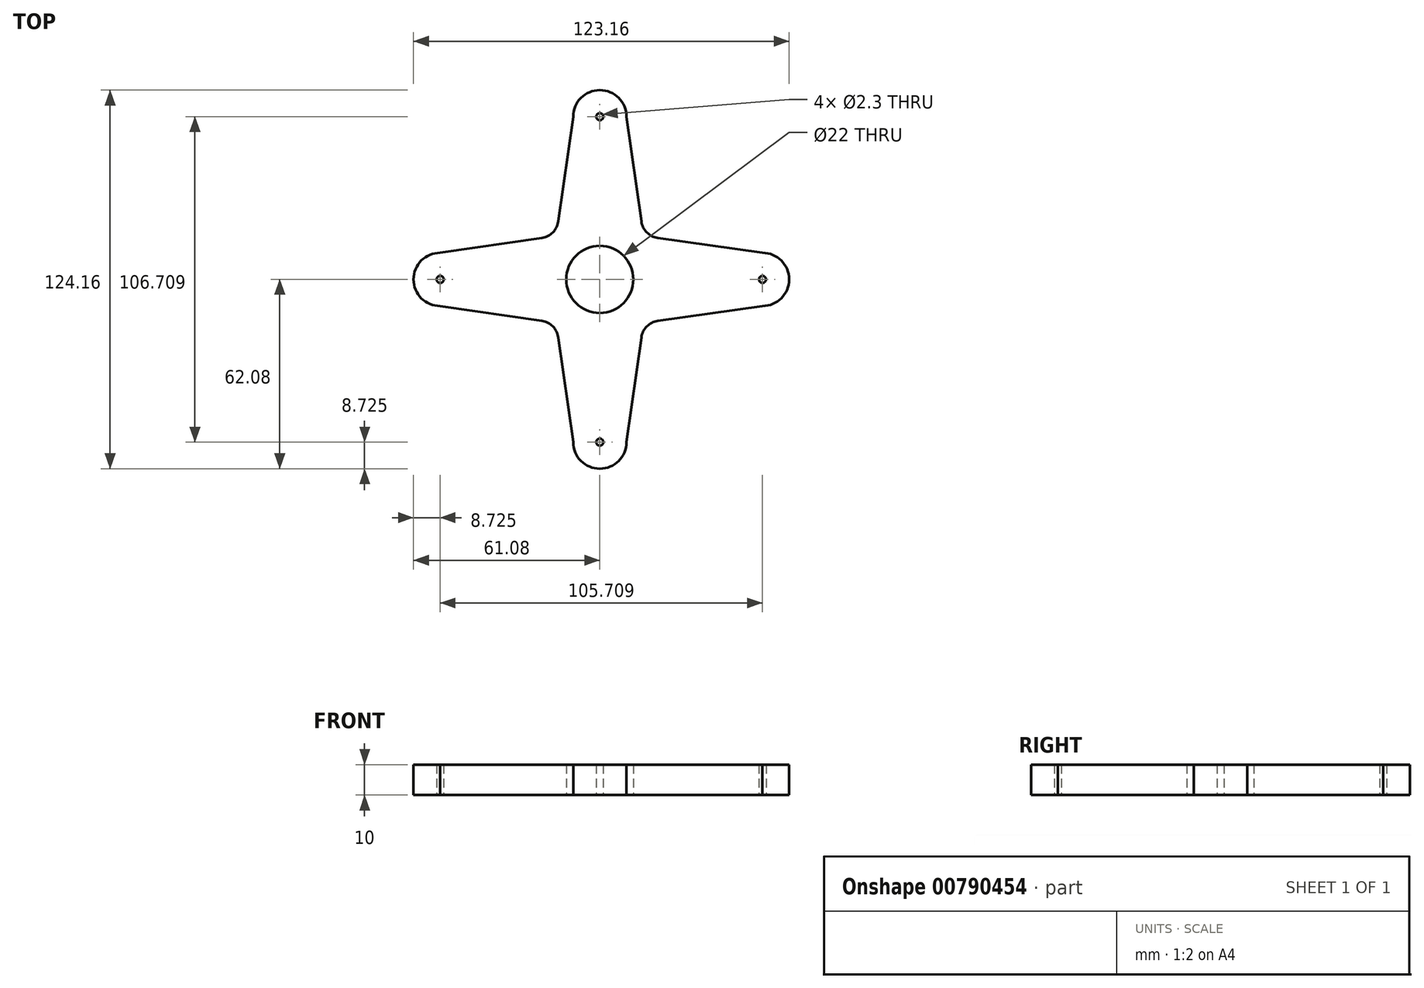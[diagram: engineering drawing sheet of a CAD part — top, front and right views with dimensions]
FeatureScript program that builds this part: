
annotation { "Feature Type Name" : "Feature", "Feature Type Description" : "" }
export const myFeature = defineFeature(function(context is Context, id is Id, definition is map)
    precondition{}
    {
        {
            var Q0;
            Q0=qCreatedBy(makeId("Top.planeOp"),FACE);
            var sketch = newSketch(context, id + "F0", { "sketchPlane" : qUnion([Q0])});
            skCircle(sketch, "E0", {"center": v(0, 0) * mm, "radius": 11 * mm});
            skCircle(sketch, "E1", {"center": v(0, 53.35) * mm, "radius": 8.73 * mm});
            skCircle(sketch, "E2.1.1", {"center": v(-52.35, 0) * mm, "radius": 8.73 * mm});
            skCircle(sketch, "E2.2.1", {"center": v(0, -53.35) * mm, "radius": 8.73 * mm});
            skCircle(sketch, "E2.3.1", {"center": v(53.35, 0) * mm, "radius": 8.73 * mm});
            skCircle(sketch, "E3", {"center": v(0, 53.35) * mm, "radius": 1.15 * mm});
            skCircle(sketch, "E4.2.0", {"center": v(0, -53.35) * mm, "radius": 1.15 * mm});
            skCircle(sketch, "E4.3.0", {"center": v(53.35, 0) * mm, "radius": 1.15 * mm});
            skLineSegment(sketch, "E5", {"start": v(8.73, 53.35) * mm, "end": v(13.62, 19) * mm});
            skLineSegment(sketch, "E6", {"start": v(-8.73, 53.35) * mm, "end": v(-13.62, 19) * mm});
            skLineSegment(sketch, "E7", {"start": v(-13.62, -19) * mm, "end": v(-8.73, -53.35) * mm});
            skLineSegment(sketch, "E8", {"start": v(13.62, -19) * mm, "end": v(8.73, -53.35) * mm});
            skLineSegment(sketch, "E9", {"start": v(53.35, 8.73) * mm, "end": v(19, 13.62) * mm});
            skLineSegment(sketch, "E10", {"start": v(53.35, -8.73) * mm, "end": v(19, -13.62) * mm});
            skArc(sketch, "E11.filletArc", {"start": v(-19, 13.62) * mm, "mid": v(-15.41, 15.41) * mm, "end": v(-13.62, 19) * mm});
            skArc(sketch, "E12.filletArc", {"start": v(13.62, 19) * mm, "mid": v(15.41, 15.41) * mm, "end": v(19, 13.62) * mm});
            skArc(sketch, "E13.filletArc", {"start": v(19, -13.62) * mm, "mid": v(15.41, -15.41) * mm, "end": v(13.62, -19) * mm});
            skArc(sketch, "E14.filletArc", {"start": v(-13.62, -19) * mm, "mid": v(-15.41, -15.41) * mm, "end": v(-19, -13.62) * mm});
            skCircle(sketch, "E15", {"center": v(-52.35, 0) * mm, "radius": 1.15 * mm});
            skLineSegment(sketch, "E16", {"start": v(-19, 13.62) * mm, "end": v(-52.35, 8.73) * mm});
            skLineSegment(sketch, "E17", {"start": v(-19, -13.62) * mm, "end": v(-52.35, -8.73) * mm});
            skSolve(sketch);
        }
        {
            var Q0;
            Q0=makeQuery(id+"F0.imprint","IMPRINT",FACE,{"disambiguationData":[TD([[makeQuery(id+"F0.imprint","IMPRINT",EDGE,{"derivedFrom":sQuery(id+"F0.wireOp",EDGE,"E0")}),-1.0]])]});
            var Q1;
            Q1=makeQuery(id+"F0.imprint","IMPRINT",FACE,{"disambiguationData":[TD([[makeQuery(id+"F0.imprint","IMPRINT",EDGE,{"derivedFrom":sQuery(id+"F0.wireOp",EDGE,"E4.2.0")}),-1.0]])]});
            var Q2;
            Q2=makeQuery(id+"F0.imprint","IMPRINT",FACE,{"disambiguationData":[TD([[makeQuery(id+"F0.imprint","IMPRINT",EDGE,{"derivedFrom":sQuery(id+"F0.wireOp",EDGE,"E15")}),-1.0]])]});
            var Q3;
            Q3=makeQuery(id+"F0.imprint","IMPRINT",FACE,{"disambiguationData":[TD([[makeQuery(id+"F0.imprint","IMPRINT",EDGE,{"derivedFrom":sQuery(id+"F0.wireOp",EDGE,"E3")}),-1.0]])]});
            var Q4;
            Q4=makeQuery(id+"F0.imprint","IMPRINT",FACE,{"disambiguationData":[TD([[makeQuery(id+"F0.imprint","IMPRINT",EDGE,{"derivedFrom":sQuery(id+"F0.wireOp",EDGE,"E4.3.0")}),-1.0]])]});
            extrude(context, id + "F1", {"entities" : qUnion([Q0, Q1, Q2, Q3, Q4]), "depth" : 10 * mm, "offsetDistance" : 25 * mm});
        }
    });
